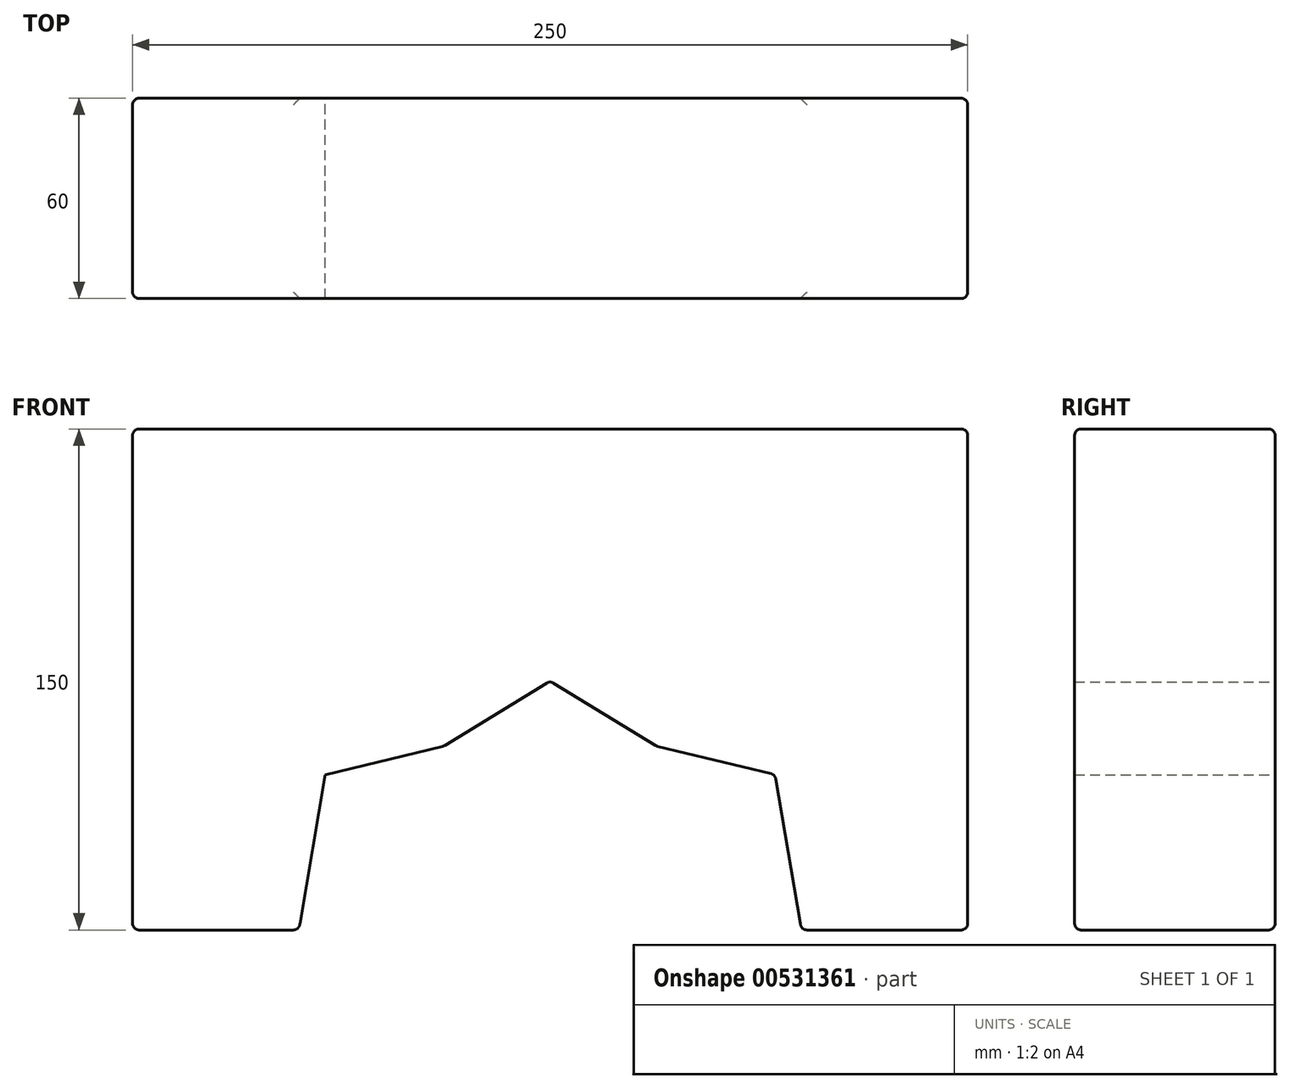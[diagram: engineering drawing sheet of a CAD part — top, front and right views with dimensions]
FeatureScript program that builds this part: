
annotation { "Feature Type Name" : "Feature", "Feature Type Description" : "" }
export const myFeature = defineFeature(function(context is Context, id is Id, definition is map)
    precondition{}
    {
        {
            var Q0;
            Q0=qCreatedBy(makeId("Front.planeOp"),FACE);
            var sketch = newSketch(context, id + "F0", { "sketchPlane" : qUnion([Q0])});
            skLineSegment(sketch, "E0", {"start": v(0, 0) * mm, "end": v(-125, 0) * mm});
            skLineSegment(sketch, "E1", {"start": v(-125, 0) * mm, "end": v(-125, 150) * mm});
            skLineSegment(sketch, "E2", {"start": v(-125, 150) * mm, "end": v(125, 150) * mm});
            skLineSegment(sketch, "E3", {"start": v(125, 150) * mm, "end": v(125, 0) * mm});
            skLineSegment(sketch, "E4", {"start": v(125, 0) * mm, "end": v(0, 0) * mm});
            skSolve(sketch);
        }
        {
            var Q0;
            Q0=makeQuery(id+"F0.imprint","IMPRINT",FACE,{"disambiguationData":[TD([[makeQuery(id+"F0.imprint","IMPRINT",EDGE,{"derivedFrom":sQuery(id+"F0.wireOp",EDGE,"E0")}),-1.0]])]});
            extrude(context, id + "F1", {"entities" : qUnion([Q0]), "depth" : 60 * mm, "offsetDistance" : 25 * mm});
        }
        {
            var Q0;
            Q0=qCreatedBy(makeId("Front.planeOp"),FACE);
            var sketch = newSketch(context, id + "F2", { "sketchPlane" : qUnion([Q0])});
            skLineSegment(sketch, "E5", {"start": v(-75.2, 0) * mm, "end": v(-67.38, 46.47) * mm});
            skLineSegment(sketch, "E6", {"start": v(-67.38, 46.47) * mm, "end": v(-31.83, 55.07) * mm});
            skLineSegment(sketch, "E7", {"start": v(-31.83, 55.07) * mm, "end": v(0, 74.56) * mm});
            skLineSegment(sketch, "E8.MirrorCS", {"start": v(31.83, 55.07) * mm, "end": v(0, 74.56) * mm});
            skLineSegment(sketch, "E9.MirrorCS", {"start": v(75.2, 0) * mm, "end": v(67.38, 46.47) * mm});
            skLineSegment(sketch, "E10.MirrorCS", {"start": v(67.38, 46.47) * mm, "end": v(31.83, 55.07) * mm});
            skLineSegment(sketch, "E11", {"start": v(-75.2, 0) * mm, "end": v(75.2, 0) * mm});
            skSolve(sketch);
        }
        {
            var Q0;
            Q0 = qSketchRegion(id + "F2", true);
            extrude(context, id + "F3", {"entities" : qUnion([Q0]), "operationType" : NewBodyOperationType.REMOVE, "depth" : 60 * mm, "offsetDistance" : 25 * mm});
        }
        {
            var Q0;
            Q0=makeQuery(id+"F1.opExtrude","CAP_EDGE",EDGE,{"disambiguationData":[OSD([sQuery(id+"F0.wireOp",EDGE,"E1")])],"isStart":false});
            var Q1;
            Q1=makeQuery(id+"F1.opExtrude","CAP_EDGE",EDGE,{"disambiguationData":[OSD([sQuery(id+"F0.wireOp",EDGE,"E2")])],"isStart":false});
            var Q2;
            Q2=makeQuery(id+"F1.opExtrude","CAP_EDGE",EDGE,{"disambiguationData":[OSD([sQuery(id+"F0.wireOp",EDGE,"E3")])],"isStart":false});
            var Q3;
            Q3=makeQuery(id+"F1.opExtrude","SWEPT_EDGE",EDGE,{"disambiguationData":[OSD([sQuery(id+"F0.wireOp",EDGE,"E1"),sQuery(id+"F0.wireOp",EDGE,"E2")])]});
            var Q4;
            Q4=makeQuery(id+"F1.opExtrude","SWEPT_EDGE",EDGE,{"disambiguationData":[OSD([sQuery(id+"F0.wireOp",EDGE,"E2"),sQuery(id+"F0.wireOp",EDGE,"E3")])]});
            var Q5;
            Q5=makeQuery(id+"F1.opExtrude","CAP_EDGE",EDGE,{"disambiguationData":[OSD([sQuery(id+"F0.wireOp",EDGE,"E2")])],"isStart":true});
            var Q6;
            Q6=makeQuery(id+"F1.opExtrude","CAP_EDGE",EDGE,{"disambiguationData":[OSD([sQuery(id+"F0.wireOp",EDGE,"E1")])],"isStart":true});
            var Q7;
            Q7=makeQuery(id+"F1.opExtrude","SWEPT_EDGE",EDGE,{"disambiguationData":[OSD([sQuery(id+"F0.wireOp",EDGE,"E0"),sQuery(id+"F0.wireOp",EDGE,"E1")])]});
            var Q8;
            Q8=makeQuery(id+"F1.opExtrude","CAP_EDGE",EDGE,{"disambiguationData":[OSD([sQuery(id+"F0.wireOp",EDGE,"E3")])],"isStart":true});
            var Q9;
            Q9=makeQuery(id+"F1.opExtrude","SWEPT_EDGE",EDGE,{"disambiguationData":[OSD([sQuery(id+"F0.wireOp",EDGE,"E3"),sQuery(id+"F0.wireOp",EDGE,"E4")])]});
            var Q10;
            {var subQ0=sQuery(id+"F0.wireOp",EDGE,"E4");var subQ1=sQuery(id+"F0.wireOp",EDGE,"E3");var subQ2=sQuery(id+"F0.wireOp",EDGE,"E0");Q10=makeQuery(id+"F3.boolean.opBoolean","SPLIT",EDGE,{"disambiguationData":[TD([makeQuery(id+"F1.opExtrude","SWEPT_FACE",FACE,{"disambiguationData":[OSD([subQ1])]})])],"derivedFrom":makeQuery(id+"F1.opExtrude","CAP_EDGE",EDGE,{"disambiguationData":[OSD([subQ2,subQ0])],"isStart":true})});}
            var Q11;
            Q11=makeQuery(id+"F3.boolean.opBoolean","COPY",EDGE,{"derivedFrom":makeQuery(id+"F3.opExtrude","SWEPT_EDGE",EDGE,{"disambiguationData":[OSD([sQuery(id+"F2.wireOp",EDGE,"E9.MirrorCS"),sQuery(id+"F2.wireOp",EDGE,"E11")])]})});
            var Q12;
            {var subQ0=sQuery(id+"F0.wireOp",EDGE,"E4");var subQ1=sQuery(id+"F0.wireOp",EDGE,"E3");var subQ2=sQuery(id+"F0.wireOp",EDGE,"E0");Q12=makeQuery(id+"F3.boolean.opBoolean","SPLIT",EDGE,{"disambiguationData":[TD([makeQuery(id+"F1.opExtrude","SWEPT_FACE",FACE,{"disambiguationData":[OSD([subQ1])]})])],"derivedFrom":makeQuery(id+"F1.opExtrude","CAP_EDGE",EDGE,{"disambiguationData":[OSD([subQ2,subQ0])],"isStart":false})});}
            var Q13;
            {var subQ0=sQuery(id+"F0.wireOp",EDGE,"E4");var subQ1=sQuery(id+"F0.wireOp",EDGE,"E1");var subQ2=sQuery(id+"F0.wireOp",EDGE,"E0");Q13=makeQuery(id+"F3.boolean.opBoolean","SPLIT",EDGE,{"disambiguationData":[TD([makeQuery(id+"F1.opExtrude","SWEPT_FACE",FACE,{"disambiguationData":[OSD([subQ1])]})])],"derivedFrom":makeQuery(id+"F1.opExtrude","CAP_EDGE",EDGE,{"disambiguationData":[OSD([subQ2,subQ0])],"isStart":false})});}
            var Q14;
            Q14=makeQuery(id+"F3.boolean.opBoolean","COPY",EDGE,{"derivedFrom":makeQuery(id+"F3.opExtrude","CAP_EDGE",EDGE,{"disambiguationData":[OSD([sQuery(id+"F2.wireOp",EDGE,"E5")])],"isStart":false})});
            var Q15;
            Q15=makeQuery(id+"F3.boolean.opBoolean","COPY",EDGE,{"derivedFrom":makeQuery(id+"F3.opExtrude","CAP_EDGE",EDGE,{"disambiguationData":[OSD([sQuery(id+"F2.wireOp",EDGE,"E6")])],"isStart":false})});
            var Q16;
            Q16=makeQuery(id+"F3.boolean.opBoolean","COPY",EDGE,{"derivedFrom":makeQuery(id+"F3.opExtrude","CAP_EDGE",EDGE,{"disambiguationData":[OSD([sQuery(id+"F2.wireOp",EDGE,"E7")])],"isStart":false})});
            var Q17;
            Q17=makeQuery(id+"F3.boolean.opBoolean","COPY",EDGE,{"derivedFrom":makeQuery(id+"F3.opExtrude","SWEPT_EDGE",EDGE,{"disambiguationData":[OSD([sQuery(id+"F2.wireOp",EDGE,"E8.MirrorCS"),sQuery(id+"F2.wireOp",EDGE,"E10.MirrorCS")])]})});
            var Q18;
            Q18=makeQuery(id+"F3.boolean.opBoolean","COPY",EDGE,{"derivedFrom":makeQuery(id+"F3.opExtrude","SWEPT_EDGE",EDGE,{"disambiguationData":[OSD([sQuery(id+"F2.wireOp",EDGE,"E6"),sQuery(id+"F2.wireOp",EDGE,"E7")])]})});
            var Q19;
            Q19=makeQuery(id+"F3.boolean.opBoolean","COPY",EDGE,{"derivedFrom":makeQuery(id+"F3.opExtrude","SWEPT_EDGE",EDGE,{"disambiguationData":[OSD([sQuery(id+"F2.wireOp",EDGE,"E7"),sQuery(id+"F2.wireOp",EDGE,"E8.MirrorCS")])]})});
            var Q20;
            Q20=makeQuery(id+"F3.boolean.opBoolean","COPY",EDGE,{"derivedFrom":makeQuery(id+"F3.opExtrude","CAP_EDGE",EDGE,{"disambiguationData":[OSD([sQuery(id+"F2.wireOp",EDGE,"E8.MirrorCS")])],"isStart":false})});
            var Q21;
            Q21=makeQuery(id+"F3.boolean.opBoolean","COPY",EDGE,{"derivedFrom":makeQuery(id+"F3.opExtrude","CAP_EDGE",EDGE,{"disambiguationData":[OSD([sQuery(id+"F2.wireOp",EDGE,"E10.MirrorCS")])],"isStart":false})});
            var Q22;
            Q22=makeQuery(id+"F3.boolean.opBoolean","COPY",EDGE,{"derivedFrom":makeQuery(id+"F3.opExtrude","SWEPT_EDGE",EDGE,{"disambiguationData":[OSD([sQuery(id+"F2.wireOp",EDGE,"E9.MirrorCS"),sQuery(id+"F2.wireOp",EDGE,"E10.MirrorCS")])]})});
            var Q23;
            Q23=makeQuery(id+"F3.boolean.opBoolean","COPY",EDGE,{"derivedFrom":makeQuery(id+"F3.opExtrude","CAP_EDGE",EDGE,{"disambiguationData":[OSD([sQuery(id+"F2.wireOp",EDGE,"E9.MirrorCS")])],"isStart":false})});
            var Q24;
            {var subQ0=sQuery(id+"F0.wireOp",EDGE,"E4");var subQ3=sQuery(id+"F0.wireOp",EDGE,"E1");var subQ4=sQuery(id+"F0.wireOp",EDGE,"E0");Q24=makeQuery(id+"F3.boolean.opBoolean","SPLIT",FACE,{"disambiguationData":[TD([makeQuery(id+"F1.opExtrude","SWEPT_FACE",FACE,{"disambiguationData":[OSD([subQ3])]})])],"derivedFrom":makeQuery(id+"F1.opExtrude","SWEPT_FACE",FACE,{"disambiguationData":[OSD([subQ4,subQ0])]})});}
            var Q25;
            Q25=makeQuery(id+"F3.boolean.opBoolean","COPY",EDGE,{"derivedFrom":makeQuery(id+"F3.opExtrude","CAP_EDGE",EDGE,{"disambiguationData":[OSD([sQuery(id+"F2.wireOp",EDGE,"E9.MirrorCS")])],"isStart":true})});
            var Q26;
            Q26=makeQuery(id+"F3.boolean.opBoolean","COPY",EDGE,{"derivedFrom":makeQuery(id+"F3.opExtrude","CAP_EDGE",EDGE,{"disambiguationData":[OSD([sQuery(id+"F2.wireOp",EDGE,"E8.MirrorCS")])],"isStart":true})});
            var Q27;
            Q27=makeQuery(id+"F3.boolean.opBoolean","COPY",EDGE,{"derivedFrom":makeQuery(id+"F3.opExtrude","CAP_EDGE",EDGE,{"disambiguationData":[OSD([sQuery(id+"F2.wireOp",EDGE,"E10.MirrorCS")])],"isStart":true})});
            var Q28;
            Q28=makeQuery(id+"F3.boolean.opBoolean","COPY",EDGE,{"derivedFrom":makeQuery(id+"F3.opExtrude","CAP_EDGE",EDGE,{"disambiguationData":[OSD([sQuery(id+"F2.wireOp",EDGE,"E7")])],"isStart":true})});
            var Q29;
            Q29=makeQuery(id+"F3.boolean.opBoolean","COPY",EDGE,{"derivedFrom":makeQuery(id+"F3.opExtrude","CAP_EDGE",EDGE,{"disambiguationData":[OSD([sQuery(id+"F2.wireOp",EDGE,"E6")])],"isStart":true})});
            var Q30;
            Q30=makeQuery(id+"F3.boolean.opBoolean","COPY",EDGE,{"derivedFrom":makeQuery(id+"F3.opExtrude","CAP_EDGE",EDGE,{"disambiguationData":[OSD([sQuery(id+"F2.wireOp",EDGE,"E5")])],"isStart":true})});
            fillet(context, id + "F4", {"entities" : qUnion([Q0, Q1, Q2, Q3, Q4, Q5, Q6, Q7, Q8, Q9, Q10, Q11, Q12, Q13, Q14, Q15, Q16, Q17, Q18, Q19, Q20, Q21, Q22, Q23, Q24, Q25, Q26, Q27, Q28, Q29, Q30]), "radius" : 2 * mm, "tangentPropagation" : true, "allowEdgeOverflow" : false});
        }
    });
